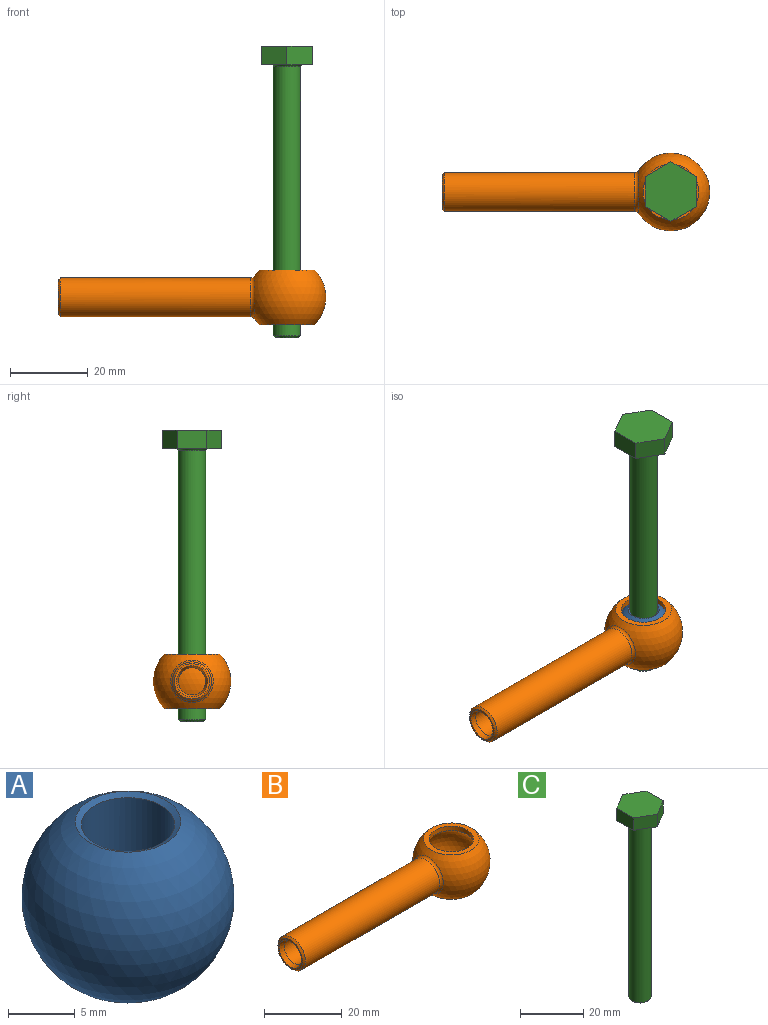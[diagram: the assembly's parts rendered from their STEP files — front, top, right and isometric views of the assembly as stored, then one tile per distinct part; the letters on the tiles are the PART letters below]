
ASSEMBLY  parts=3 mates=2
PART A: 4 faces, bbox 16x16x13.9 mm
  f0: sphere r=7.99mm, area 696.3mm2, adj f2,f3
  f1: cylinder r=3.5mm len=13.33mm, axis (0,0,1), area 293.1mm2, adj f2,f3
  f2: cone r=3.97mm half-angle=59.9deg, axis (0,0,-1), area 12.7mm2, adj f0,f1
  f3: cone r=3.5mm half-angle=59.9deg, axis (0,0,1), area 12.7mm2, adj f0,f1
PART B: 13 faces, bbox 68.7x20x14 mm
  f0: cylinder r=5mm len=48.94mm, axis (1,0,0), area 1537.5mm2, adj f10,f11
  f1: plane 9x9mm, normal (-1,0,0), area 13.4mm2, adj f11,f12
  f2: cylinder r=3.5mm len=47.99mm, axis (1,0,0), area 1055.4mm2, adj f3,f12
  f3: sphere r=10mm, area 39.7mm2, adj f2
  f4: sphere r=10mm, area 777.9mm2, adj f5,f6,f10
  f5: plane 14.28x14.28mm, normal (0,0,-1), area 57.7mm2, adj f4,f9
  f6: plane 14.28x14.28mm, normal (0,0,1), area 57.7mm2, adj f4,f7
  f7: cylinder r=5.71mm len=11.43mm, axis (0,0,1), area 50.3mm2, adj f6,f8
  f8: sphere r=8mm, area 563mm2, adj f7,f9
  f9: cylinder r=5.71mm len=11.43mm, axis (0,0,1), area 50.3mm2, adj f5,f8
  f10: torus R=6mm, axis (1,0,0), area 32.2mm2, adj f0,f4
  f11: cone r=5mm half-angle=45deg, axis (1,0,0), area 21.1mm2, adj f0,f1
  f12: cone r=4mm half-angle=21deg, axis (-1,0,0), area 32.8mm2, adj f1,f2
PART C: 12 faces, bbox 13.2x15.3x74.8 mm
  f0: cylinder r=3.5mm len=69mm, axis (0,0,-1), area 1517.4mm2, adj f10,f11
  f1: plane 6x6mm, normal (0,0,-1), area 28.3mm2, adj f11
  f2: plane 6.62x4.8mm, normal (-0.5,0.87,0), area 36.7mm2, adj f3,f7,f8,f9
  f3: plane 7.65x4.8mm, normal (-1,0,0), area 36.7mm2, adj f2,f4,f8,f9
  f4: plane 6.62x4.8mm, normal (-0.5,-0.87,0), area 36.7mm2, adj f3,f5,f8,f9
  f5: plane 6.62x4.8mm, normal (0.5,-0.87,0), area 36.7mm2, adj f4,f6,f8,f9
  f6: plane 7.65x4.8mm, normal (1,0,0), area 36.7mm2, adj f5,f7,f8,f9
  f7: plane 6.62x4.8mm, normal (0.5,0.87,0), area 36.7mm2, adj f2,f6,f8,f9
  f8: plane 15.29x13.24mm, normal (0,0,1), area 151.8mm2, adj f2,f3,f4,f5,f6,f7
  f9: plane 15.29x13.24mm, normal (0,0,-1), area 101.6mm2, adj f2,f3,f4,f5,f6,f7,f10
  f10: torus R=4mm, axis (0,0,1), area 18.2mm2, adj f0,f9
  f11: cone r=3mm half-angle=45deg, axis (0,0,1), area 14.4mm2, adj f0,f1
PLACE A t=(-4.16,15.48,26.82)mm
PLACE B t=(-4.16,15.48,26.82)mm
PLACE C t=(-4.16,15.48,26.82)mm
MATE cylindrical C.f0 <-> A.f2  axis (0,0,-1) through (-4.16,15.48,26.82)mm
MATE ball B.f7 <-> A.f2  axis (0,0,-1) through (-4.16,15.48,26.82)mm
